# Revit family: QUADROP-S-xxFSWxxxM0200
name_source: partatom
category: Leuchten
units: mm (PartAtom-declared; Revit-internal decimal feet)

## family parameters
Basisbauteil = Fläche
Beim Laden mit Abzugskörper schneiden = Nein
Bemaßung runder Anschluss = Durchmesser verwenden
Gemeinsam genutzt = Nein
Lichtquelle = Ja
OmniClass-Nummer = 23.80.70.11
OmniClass-Titel = Luminaries for Internal Lighting
Raumberechnungspunkt = Nein
Teiletyp = Normal

## types (4) — shared parameters
Baugruppenkennzeichen = D5020200
Datei für fotometrisches Netz = QUADROP-S DAFSW840M0200.IES
Emissionsform beim Rendern sichtbar = Nein
Farbfilter = 16777215
Farbtemperaturverschiebung bei Dämpfen der Lampe = <Keine Auswahl>
Hersteller = RIDI Leuchten GmbH
Lampe = LED
Neigungswinkel = 90.00°
Scheinlast = 19 VA
URL = www.spectral.de
Von Breite des Rechtecks ausssenden = 78 mm  [stored 0.255906 ft]
Von Länge des Rechtecks aussenden = 78 mm  [stored 0.255906 ft]
brand = Spectral
conformity mark = CE
electrical safety class = 1
height = 58 mm  [stored 0.190289 ft]
ingress protection (IP) code = IP20
length = 145 mm  [stored 0.475722 ft]
nominal frequency = 50-60Hz
nominal voltage = 230
rated input power = 19
voltage type (AC, DC, UC) = AC
weight = 0,6 kg
width = 145 mm  [stored 0.475722 ft]
zero-valued in all types: Vorgabe-Ansicht

## per-type parameters (varying)
| type | Modell |
| QUADROP-S NDFSW830M0200 | SPG0320264AQ |
| QUADROP-S DAFSW830M0200 | SPG0330264AQ |
| QUADROP-S NDFSW840M0200 | SPG0320267AQ |
| QUADROP-S DAFSW840M0200 | SPG0330267AQ |

note: column(s) folded — value = type name in every type: product name

note: [stored X ft] marks values corroborated as IEEE doubles in the binary element streams (Revit-internal decimal feet)
